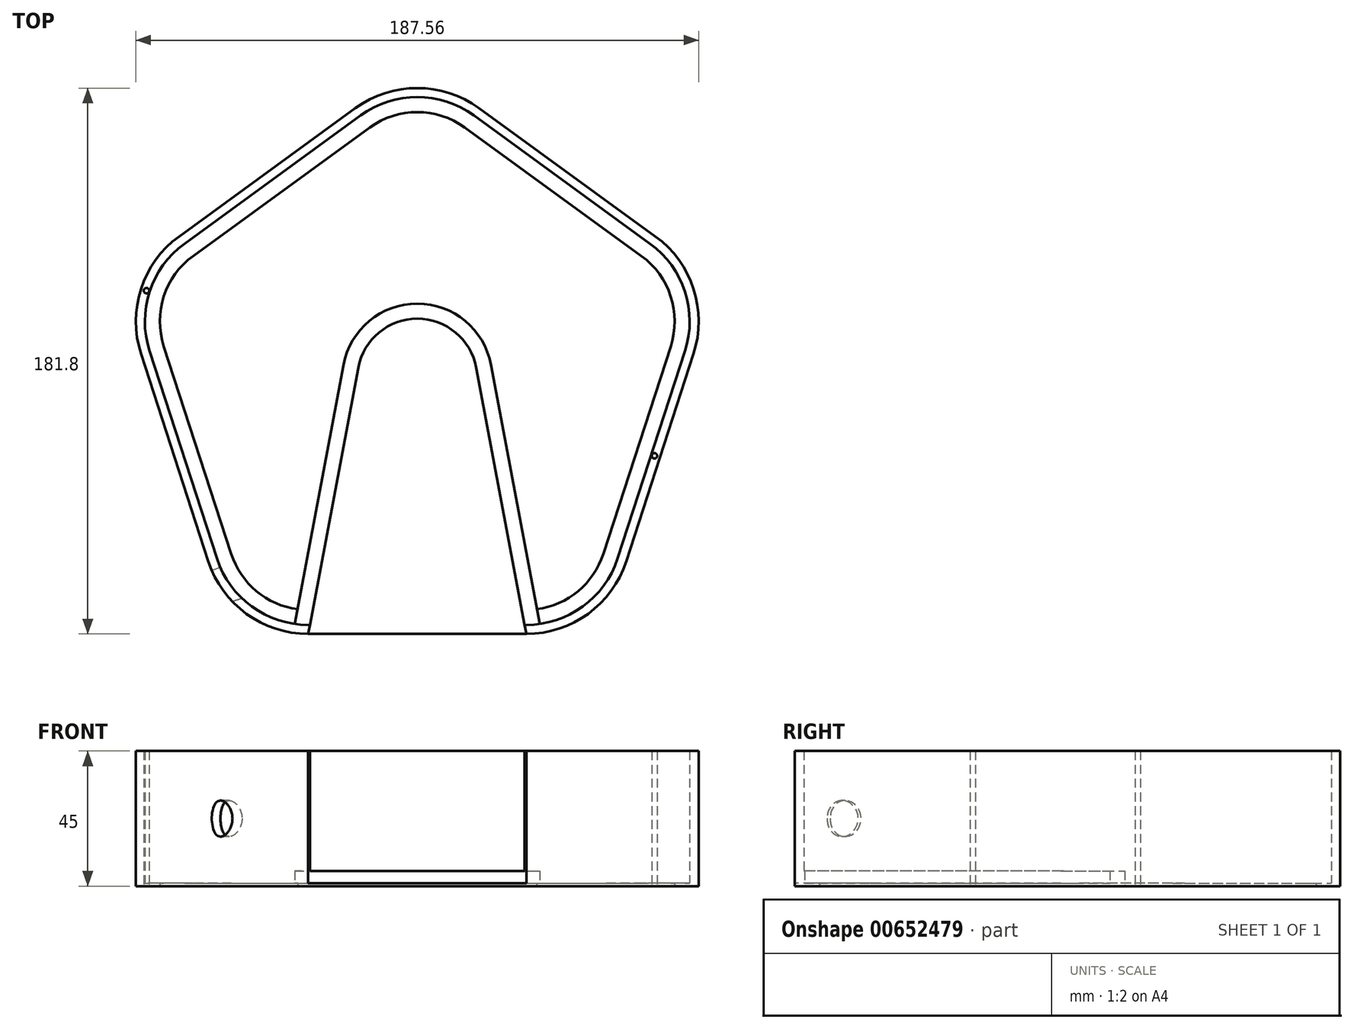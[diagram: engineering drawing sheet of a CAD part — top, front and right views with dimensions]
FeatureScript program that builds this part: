
annotation { "Feature Type Name" : "Feature", "Feature Type Description" : "" }
export const myFeature = defineFeature(function(context is Context, id is Id, definition is map)
    precondition{}
    {
        {
            var Q0;
            Q0=qCreatedBy(makeId("Top.planeOp"),FACE);
            var sketch = newSketch(context, id + "F0", { "sketchPlane" : qUnion([Q0])});
            skCircle(sketch, "E0.cCircle", {"center": v(0, 0) * mm, "radius": 85 * mm, "construction": true});
            skLineSegment(sketch, "E0.0", {"start": v(92.07, 8.28) * mm, "end": v(69.61, -60.82) * mm});
            skLineSegment(sketch, "E0.1", {"start": v(36.33, -85) * mm, "end": v(-36.33, -85) * mm});
            skLineSegment(sketch, "E0.2", {"start": v(-69.61, -60.82) * mm, "end": v(-92.07, 8.28) * mm});
            skLineSegment(sketch, "E0.3", {"start": v(-79.35, 47.41) * mm, "end": v(-20.57, 90.12) * mm});
            skLineSegment(sketch, "E0.4", {"start": v(20.57, 90.12) * mm, "end": v(79.35, 47.41) * mm});
            skPoint(sketch, "E0.0.midPoint", {"position": v(80.84, -26.27) * mm});
            skPoint(sketch, "E1.visualSharp", {"position": v(-99.92, 32.47) * mm});
            skArc(sketch, "E1.filletArc", {"start": v(-79.35, 47.41) * mm, "mid": v(-92.07, 29.91) * mm, "end": v(-92.07, 8.28) * mm});
            skPoint(sketch, "E2.visualSharp", {"position": v(-61.76, -85) * mm});
            skArc(sketch, "E2.filletArc", {"start": v(-69.61, -60.82) * mm, "mid": v(-56.9, -78.32) * mm, "end": v(-36.33, -85) * mm});
            skPoint(sketch, "E3.visualSharp", {"position": v(61.76, -85) * mm});
            skArc(sketch, "E3.filletArc", {"start": v(36.33, -85) * mm, "mid": v(56.9, -78.32) * mm, "end": v(69.61, -60.82) * mm});
            skPoint(sketch, "E4.visualSharp", {"position": v(99.92, 32.47) * mm});
            skArc(sketch, "E4.filletArc", {"start": v(92.07, 8.28) * mm, "mid": v(92.07, 29.91) * mm, "end": v(79.35, 47.41) * mm});
            skPoint(sketch, "E5.visualSharp", {"position": v(0, 105.07) * mm});
            skArc(sketch, "E5.filletArc", {"start": v(20.57, 90.12) * mm, "mid": v(0, 96.8) * mm, "end": v(-20.57, 90.12) * mm});
            skArc(sketch, "E6.0", {"start": v(89.21, 9.2) * mm, "mid": v(89.21, 28.99) * mm, "end": v(77.59, 44.99) * mm});
            skLineSegment(sketch, "E6.1", {"start": v(18.8, 87.7) * mm, "end": v(77.59, 44.99) * mm});
            skLineSegment(sketch, "E6.2", {"start": v(89.21, 9.2) * mm, "end": v(66.76, -59.89) * mm});
            skArc(sketch, "E6.3", {"start": v(18.8, 87.7) * mm, "mid": v(0, 93.8) * mm, "end": v(-18.8, 87.7) * mm});
            skLineSegment(sketch, "E6.4", {"start": v(-77.59, 44.99) * mm, "end": v(-18.8, 87.7) * mm});
            skArc(sketch, "E6.5", {"start": v(-77.59, 44.99) * mm, "mid": v(-89.21, 28.99) * mm, "end": v(-89.21, 9.2) * mm});
            skArc(sketch, "E6.6", {"start": v(36.33, -82) * mm, "mid": v(55.14, -75.89) * mm, "end": v(66.76, -59.89) * mm});
            skLineSegment(sketch, "E6.7", {"start": v(36.33, -82) * mm, "end": v(-36.33, -82) * mm});
            skArc(sketch, "E6.8", {"start": v(-66.76, -59.89) * mm, "mid": v(-55.14, -75.89) * mm, "end": v(-36.33, -82) * mm});
            skLineSegment(sketch, "E6.9", {"start": v(-66.76, -59.89) * mm, "end": v(-89.21, 9.2) * mm});
            skCircle(sketch, "E7", {"center": v(-90.26, 29.33) * mm, "radius": 0.9 * mm});
            skCircle(sketch, "E8", {"center": v(79.03, -25.68) * mm, "radius": 0.9 * mm});
            skPoint(sketch, "E9", {"position": v(-89.21, 28.99) * mm});
            skLineSegment(sketch, "E10.0", {"start": v(-89.21, 28.99) * mm, "end": v(-90.26, 29.33) * mm, "construction": true});
            skLineSegment(sketch, "E11.0", {"start": v(80.84, -26.27) * mm, "end": v(0, 0) * mm, "construction": true});
            skArc(sketch, "E12", {"start": v(19.66, 3.7) * mm, "mid": v(0, 20) * mm, "end": v(-19.66, 3.7) * mm});
            skLineSegment(sketch, "E13", {"start": v(-19.66, 3.7) * mm, "end": v(-36.33, -85) * mm});
            skLineSegment(sketch, "E14", {"start": v(19.66, 3.7) * mm, "end": v(36.33, -85) * mm});
            skArc(sketch, "E15.0", {"start": v(-62, -58.34) * mm, "mid": v(-52.2, -71.84) * mm, "end": v(-36.33, -77) * mm});
            skLineSegment(sketch, "E15.1", {"start": v(36.33, -77) * mm, "end": v(-36.33, -77) * mm});
            skLineSegment(sketch, "E15.2", {"start": v(-62, -58.34) * mm, "end": v(-84.46, 10.75) * mm});
            skArc(sketch, "E15.3", {"start": v(36.33, -77) * mm, "mid": v(52.2, -71.84) * mm, "end": v(62, -58.34) * mm});
            skLineSegment(sketch, "E15.4", {"start": v(84.46, 10.75) * mm, "end": v(62, -58.34) * mm});
            skArc(sketch, "E15.5", {"start": v(84.46, 10.75) * mm, "mid": v(84.46, 27.44) * mm, "end": v(74.65, 40.94) * mm});
            skArc(sketch, "E15.6", {"start": v(-74.65, 40.94) * mm, "mid": v(-84.46, 27.44) * mm, "end": v(-84.46, 10.75) * mm});
            skLineSegment(sketch, "E15.7", {"start": v(-74.65, 40.94) * mm, "end": v(-15.87, 83.65) * mm});
            skArc(sketch, "E15.8", {"start": v(15.87, 83.65) * mm, "mid": v(0, 88.8) * mm, "end": v(-15.87, 83.65) * mm});
            skLineSegment(sketch, "E15.9", {"start": v(15.87, 83.65) * mm, "end": v(74.65, 40.94) * mm});
            skLineSegment(sketch, "E16.0", {"start": v(-24.57, 4.62) * mm, "end": v(-41.24, -84.08) * mm});
            skArc(sketch, "E16.1", {"start": v(24.57, 4.62) * mm, "mid": v(0, 25) * mm, "end": v(-24.57, 4.62) * mm});
            skLineSegment(sketch, "E16.2", {"start": v(24.57, 4.62) * mm, "end": v(41.24, -84.08) * mm});
            skSolve(sketch);
        }
        {
            var Q0;
            Q0=makeQuery(id+"F0.imprint","IMPRINT",FACE,{"disambiguationData":[TD([[makeQuery(id+"F0.imprint","IMPRINT",EDGE,{"derivedFrom":sQuery(id+"F0.wireOp",EDGE,"E0.0")}),-1.0]])]});
            extrude(context, id + "F1", {"entities" : qUnion([Q0]), "depth" : 45 * mm, "offsetDistance" : 25 * mm});
        }
        {
            var Q0;
            {var subQ6=sQuery(id+"F0.wireOp",EDGE,"E12");Q0=makeQuery(id+"F0.imprint","IMPRINT",FACE,{"disambiguationData":[TD([[makeQuery(id+"F0.imprint","IMPRINT",EDGE,{"derivedFrom":subQ6}),-1.0]])]});}
            var Q1;
            {var subQ6=sQuery(id+"F0.wireOp",EDGE,"E6.7");var subQ9=sQuery(id+"F0.wireOp",EDGE,"E6.8");var subQ10=makeQuery(id+"F0.imprint","INTERSECT",VERTEX,{"derivedFrom":[subQ6,subQ9]});Q1=makeQuery(id+"F0.imprint","IMPRINT",FACE,{"disambiguationData":[TD([[makeQuery(id+"F0.imprint","IMPRINT",EDGE,{"disambiguationData":[TD([[subQ10,1.0]])],"derivedFrom":subQ6}),-1.0]])]});}
            var Q2;
            {var subQ5=sQuery(id+"F0.wireOp",EDGE,"E6.7");var subQ6=sQuery(id+"F0.wireOp",EDGE,"E6.6");var subQ7=makeQuery(id+"F0.imprint","INTERSECT",VERTEX,{"derivedFrom":[subQ6,subQ5]});Q2=makeQuery(id+"F0.imprint","IMPRINT",FACE,{"disambiguationData":[TD([[makeQuery(id+"F0.imprint","IMPRINT",EDGE,{"disambiguationData":[TD([[subQ7,-1.0]])],"derivedFrom":subQ6}),1.0]])]});}
            extrude(context, id + "F2", {"entities" : qUnion([Q0, Q1, Q2]), "operationType" : NewBodyOperationType.ADD, "depth" : 5 * mm, "offsetDistance" : 25 * mm});
        }
        {
            var Q0;
            {var subQ0=sQuery(id+"F0.wireOp",EDGE,"E14");var subQ1=sQuery(id+"F0.wireOp",EDGE,"E6.7");var subQ2=makeQuery(id+"F0.imprint","INTERSECT",VERTEX,{"derivedFrom":[subQ1,subQ0]});Q0=makeQuery(id+"F0.imprint","IMPRINT",FACE,{"disambiguationData":[TD([[makeQuery(id+"F0.imprint","IMPRINT",EDGE,{"disambiguationData":[TD([[subQ2,-1.0]])],"derivedFrom":subQ1}),-1.0]])]});}
            var Q1;
            {var subQ0=sQuery(id+"F0.wireOp",EDGE,"E0.1");Q1=makeQuery(id+"F0.imprint","IMPRINT",FACE,{"disambiguationData":[TD([[makeQuery(id+"F0.imprint","IMPRINT",EDGE,{"derivedFrom":subQ0}),-1.0]])]});}
            var Q2;
            {var subQ0=sQuery(id+"F0.wireOp",EDGE,"E12");var subQ1=makeQuery(id+"F0.imprint","INTERSECT",VERTEX,{"derivedFrom":[subQ0,sQuery(id+"F0.wireOp",EDGE,"E13")]});Q2=makeQuery(id+"F0.imprint","IMPRINT",FACE,{"disambiguationData":[TD([[makeQuery(id+"F0.imprint","IMPRINT",EDGE,{"disambiguationData":[TD([[subQ1,1.0]])],"derivedFrom":subQ0}),1.0]])]});}
            var Q3;
            Q3=makeQuery(id+"F0.imprint","IMPRINT",FACE,{"disambiguationData":[TD([[makeQuery(id+"F0.imprint","IMPRINT",EDGE,{"derivedFrom":sQuery(id+"F0.wireOp",EDGE,"E6.0")}),1.0]])]});
            extrude(context, id + "F3", {"entities" : qUnion([Q0, Q1, Q2, Q3]), "operationType" : NewBodyOperationType.ADD, "depth" : 1 * mm, "offsetDistance" : 25 * mm});
        }
        {
            var Q0;
            Q0=makeQuery(id+"F1.opExtrude","SWEPT_FACE",FACE,{"disambiguationData":[OSD([sQuery(id+"F0.wireOp",EDGE,"E0.2")])]});
            var sketch = newSketch(context, id + "F4", { "sketchPlane" : qUnion([Q0])});
            skCircle(sketch, "E17", {"center": v(45.56, 22.5) * mm, "radius": 6 * mm});
            skPoint(sketch, "E18", {"position": v(36.33, 22.5) * mm});
            skSolve(sketch);
        }
        {
            var Q0;
            Q0=makeQuery(id+"F4.imprint","IMPRINT",FACE,{"disambiguationData":[TD([[makeQuery(id+"F4.imprint","IMPRINT",EDGE,{"derivedFrom":sQuery(id+"F4.wireOp",EDGE,"E17")}),1.0]])]});
            extrude(context, id + "F5", {"entities" : qUnion([Q0]), "operationType" : NewBodyOperationType.REMOVE, "oppositeDirection" : true, "depth" : 25 * mm, "offsetDistance" : 25 * mm});
        }
    });
